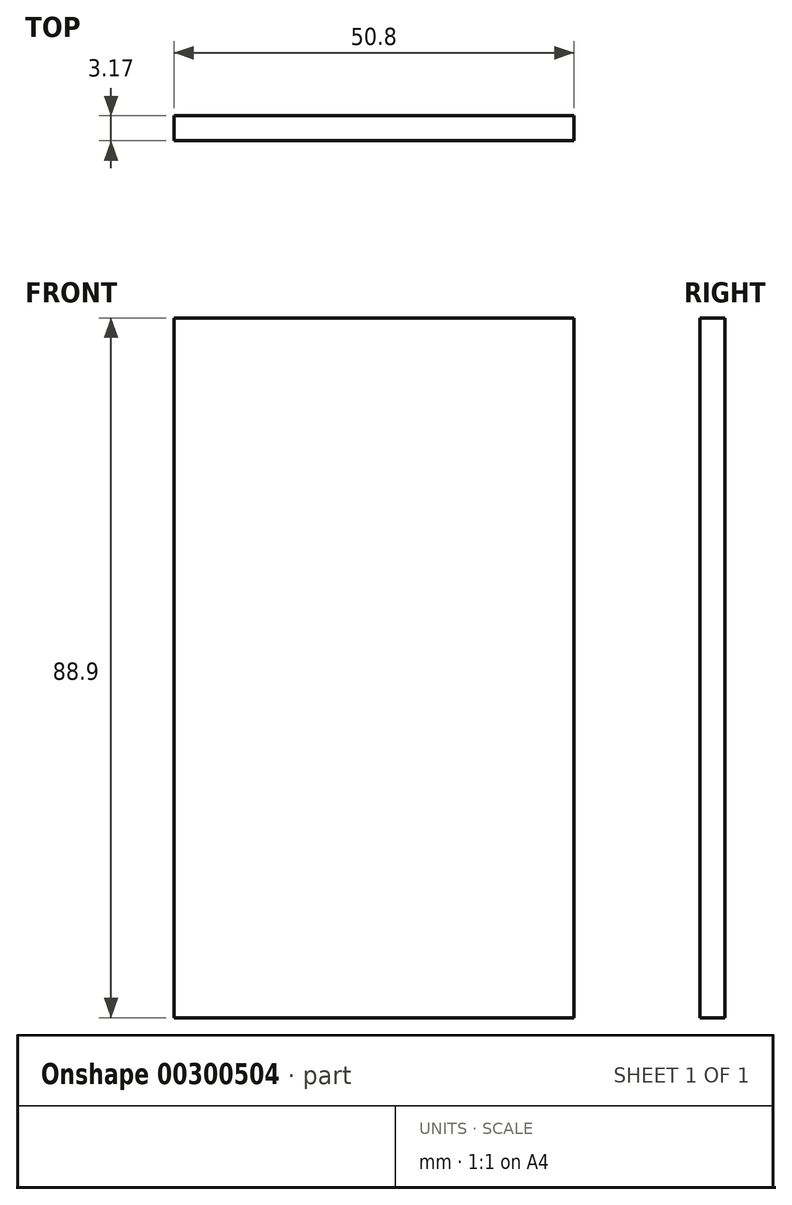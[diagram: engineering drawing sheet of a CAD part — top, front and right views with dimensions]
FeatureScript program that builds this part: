
annotation { "Feature Type Name" : "Feature", "Feature Type Description" : "" }
export const myFeature = defineFeature(function(context is Context, id is Id, definition is map)
    precondition{}
    {
        {
            var Q0;
            Q0=qCreatedBy(makeId("Front.planeOp"),FACE);
            var sketch = newSketch(context, id + "F0", { "sketchPlane" : qUnion([Q0])});
            skLineSegment(sketch, "E0.bottom", {"start": v(-25.4, 44.45) * mm, "end": v(25.4, 44.45) * mm});
            skLineSegment(sketch, "E0.top", {"start": v(-25.4, -44.45) * mm, "end": v(25.4, -44.45) * mm});
            skLineSegment(sketch, "E0.left", {"start": v(-25.4, 44.45) * mm, "end": v(-25.4, -44.45) * mm});
            skLineSegment(sketch, "E0.right", {"start": v(25.4, 44.45) * mm, "end": v(25.4, -44.45) * mm});
            skPoint(sketch, "E0.middle", {"position": v(0, 0) * mm});
            skSolve(sketch);
        }
        {
            var Q0;
            Q0 = qSketchRegion(id + "F0", true);
            extrude(context, id + "F1", {"entities" : qUnion([Q0]), "depth" : 3.17 * mm});
        }
    });
